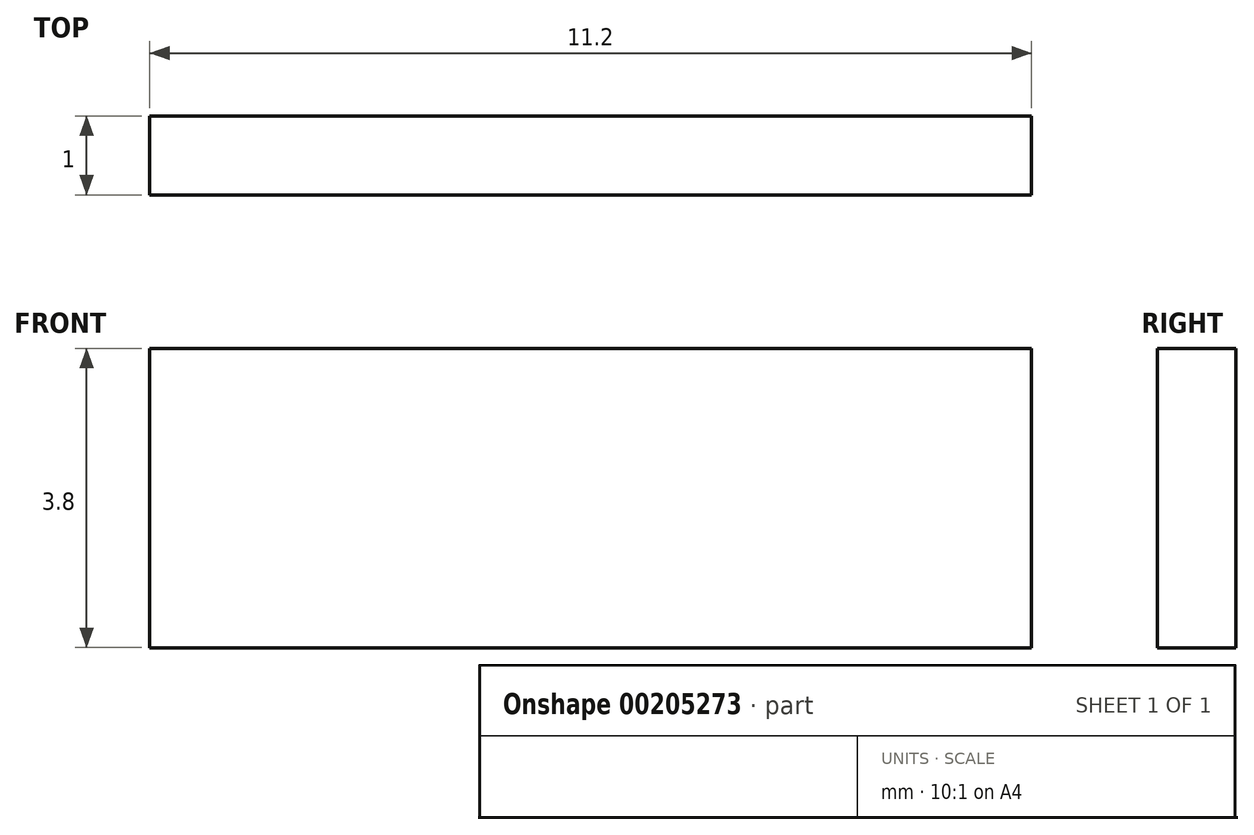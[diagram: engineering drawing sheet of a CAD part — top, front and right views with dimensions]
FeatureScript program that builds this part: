
annotation { "Feature Type Name" : "Feature", "Feature Type Description" : "" }
export const myFeature = defineFeature(function(context is Context, id is Id, definition is map)
    precondition{}
    {
        {
            var Q0;
            Q0=qCreatedBy(makeId("Front.planeOp"),FACE);
            var sketch = newSketch(context, id + "F0", { "sketchPlane" : qUnion([Q0])});
            skLineSegment(sketch, "E0.bottom", {"start": v(-40.94, 29.53) * mm, "end": v(-29.74, 29.53) * mm});
            skLineSegment(sketch, "E0.top", {"start": v(-40.94, 25.73) * mm, "end": v(-29.74, 25.73) * mm});
            skLineSegment(sketch, "E0.left", {"start": v(-40.94, 29.53) * mm, "end": v(-40.94, 25.73) * mm});
            skLineSegment(sketch, "E0.right", {"start": v(-29.74, 29.53) * mm, "end": v(-29.74, 25.73) * mm});
            skSolve(sketch);
        }
        {
            var Q0;
            Q0 = qSketchRegion(id + "F0", true);
            extrude(context, id + "F1", {"entities" : qUnion([Q0]), "depth" : 1 * mm});
        }
    });
